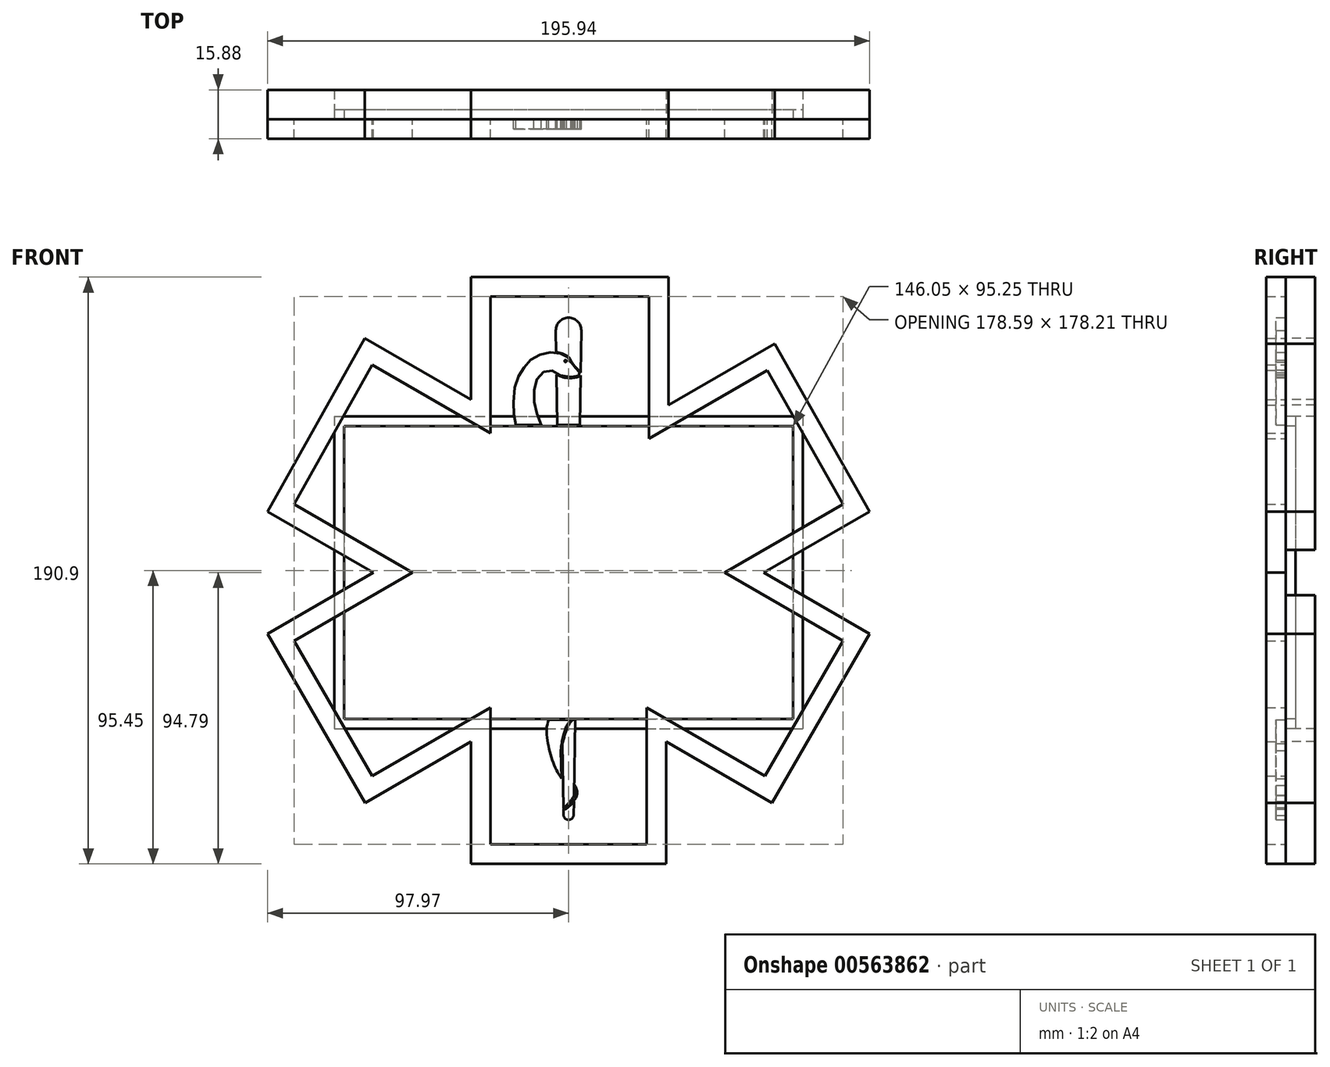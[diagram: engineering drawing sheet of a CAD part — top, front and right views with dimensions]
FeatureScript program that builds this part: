
annotation { "Feature Type Name" : "Feature", "Feature Type Description" : "" }
export const myFeature = defineFeature(function(context is Context, id is Id, definition is map)
    precondition{}
    {
        {
            var Q0;
            Q0=qCreatedBy(makeId("Front.planeOp"),FACE);
            var sketch = newSketch(context, id + "F0", { "sketchPlane" : qUnion([Q0])});
            skLineSegment(sketch, "E0.bottom", {"start": v(-76.2, 50.8) * mm, "end": v(76.2, 50.8) * mm});
            skLineSegment(sketch, "E0.top", {"start": v(-76.2, -50.8) * mm, "end": v(76.2, -50.8) * mm});
            skLineSegment(sketch, "E0.left", {"start": v(-76.2, 50.8) * mm, "end": v(-76.2, -50.8) * mm});
            skLineSegment(sketch, "E0.right", {"start": v(76.2, 50.8) * mm, "end": v(76.2, -50.8) * mm});
            skPoint(sketch, "E0.middle", {"position": v(0, 0) * mm});
            skCircle(sketch, "E1", {"center": v(0, 0) * mm, "radius": 50.8 * mm, "construction": true});
            skPoint(sketch, "E2.endSnap0", {"position": v(0, 50.8) * mm});
            skLineSegment(sketch, "E3", {"start": v(0, 50.8) * mm, "end": v(0, 173.84) * mm, "construction": true});
            skLineSegment(sketch, "E4", {"start": v(0, -50.8) * mm, "end": v(0, -189.44) * mm, "construction": true});
            skPoint(sketch, "E5.endSnap0", {"position": v(-44, 0) * mm});
            skLineSegment(sketch, "E6", {"start": v(-25.4, -44) * mm, "end": v(-25.4, -88.44) * mm});
            skLineSegment(sketch, "E7", {"start": v(-25.4, -88.44) * mm, "end": v(25.4, -88.44) * mm});
            skLineSegment(sketch, "E8", {"start": v(25.4, -88.44) * mm, "end": v(25.4, -44) * mm});
            skLineSegment(sketch, "E9", {"start": v(25.4, -44) * mm, "end": v(63.9, -66.22) * mm});
            skLineSegment(sketch, "E10", {"start": v(50.8, 0) * mm, "end": v(89.3, -22.23) * mm});
            skLineSegment(sketch, "E11", {"start": v(50.8, 0) * mm, "end": v(89.3, 22.23) * mm});
            skLineSegment(sketch, "E12", {"start": v(26.16, 43.55) * mm, "end": v(64.66, 65.77) * mm});
            skLineSegment(sketch, "E13", {"start": v(26.16, 43.55) * mm, "end": v(26.16, 89.76) * mm});
            skLineSegment(sketch, "E14", {"start": v(-25.4, 45.31) * mm, "end": v(-25.4, 89.76) * mm});
            skLineSegment(sketch, "E15", {"start": v(-25.4, 45.31) * mm, "end": v(-63.9, 67.54) * mm});
            skLineSegment(sketch, "E16", {"start": v(-50.8, 0) * mm, "end": v(-89.3, 22.23) * mm});
            skLineSegment(sketch, "E17", {"start": v(-50.8, 0) * mm, "end": v(-89.3, -22.23) * mm});
            skLineSegment(sketch, "E18", {"start": v(-25.4, -44) * mm, "end": v(-63.9, -66.22) * mm});
            skLineSegment(sketch, "E19", {"start": v(-25.4, 89.76) * mm, "end": v(26.16, 89.76) * mm});
            skLineSegment(sketch, "E20", {"start": v(64.66, 65.77) * mm, "end": v(89.3, 22.22) * mm});
            skLineSegment(sketch, "E21", {"start": v(-63.9, 67.54) * mm, "end": v(-89.3, 22.23) * mm});
            skLineSegment(sketch, "E22", {"start": v(-89.3, -22.23) * mm, "end": v(-63.9, -66.22) * mm});
            skLineSegment(sketch, "E23", {"start": v(63.9, -66.22) * mm, "end": v(89.3, -22.23) * mm});
            skLineSegment(sketch, "E24.0", {"start": v(32.51, 54.54) * mm, "end": v(67.03, 74.47) * mm});
            skLineSegment(sketch, "E24.1", {"start": v(67.03, 74.47) * mm, "end": v(97.92, 19.87) * mm});
            skLineSegment(sketch, "E24.2", {"start": v(63.5, 0) * mm, "end": v(97.92, 19.87) * mm});
            skLineSegment(sketch, "E24.3", {"start": v(63.5, 0) * mm, "end": v(97.97, -19.9) * mm});
            skLineSegment(sketch, "E24.4", {"start": v(66.22, -74.9) * mm, "end": v(97.97, -19.9) * mm});
            skLineSegment(sketch, "E24.5", {"start": v(32.51, 54.54) * mm, "end": v(32.51, 96.11) * mm});
            skLineSegment(sketch, "E24.6", {"start": v(31.75, -55) * mm, "end": v(66.22, -74.9) * mm});
            skLineSegment(sketch, "E24.7", {"start": v(31.75, -94.8) * mm, "end": v(31.75, -55) * mm});
            skLineSegment(sketch, "E24.8", {"start": v(-66.29, 76.25) * mm, "end": v(-97.9, 19.86) * mm});
            skLineSegment(sketch, "E24.9", {"start": v(-31.75, 56.31) * mm, "end": v(-66.29, 76.25) * mm});
            skLineSegment(sketch, "E24.10", {"start": v(-31.75, 56.31) * mm, "end": v(-31.75, 96.11) * mm});
            skLineSegment(sketch, "E24.11", {"start": v(-31.75, 96.11) * mm, "end": v(32.51, 96.11) * mm});
            skLineSegment(sketch, "E24.12", {"start": v(-63.5, 0) * mm, "end": v(-97.9, 19.86) * mm});
            skLineSegment(sketch, "E24.13", {"start": v(-63.5, 0) * mm, "end": v(-97.97, -19.9) * mm});
            skLineSegment(sketch, "E24.14", {"start": v(-97.97, -19.9) * mm, "end": v(-66.22, -74.9) * mm});
            skLineSegment(sketch, "E24.15", {"start": v(-31.75, -55) * mm, "end": v(-66.22, -74.9) * mm});
            skLineSegment(sketch, "E24.16", {"start": v(-31.75, -55) * mm, "end": v(-31.75, -94.8) * mm});
            skLineSegment(sketch, "E24.17", {"start": v(-31.75, -94.8) * mm, "end": v(31.75, -94.8) * mm});
            skLineSegment(sketch, "E25.0", {"start": v(-73.03, 47.63) * mm, "end": v(73.02, 47.63) * mm});
            skLineSegment(sketch, "E25.1", {"start": v(-73.03, 47.63) * mm, "end": v(-73.03, -47.62) * mm});
            skLineSegment(sketch, "E25.2", {"start": v(-73.03, -47.62) * mm, "end": v(73.03, -47.62) * mm});
            skLineSegment(sketch, "E25.3", {"start": v(73.02, 47.63) * mm, "end": v(73.02, -47.62) * mm});
            skSolve(sketch);
        }
        {
            var Q0;
            Q0=qCreatedBy(makeId("Front.planeOp"),FACE);
            var sketch = newSketch(context, id + "F1", { "sketchPlane" : qUnion([Q0])});
            skPoint(sketch, "E26", {"position": v(0, 78.78) * mm});
            skArc(sketch, "E27", {"start": v(-4.15, 78.78) * mm, "mid": v(0, 82.92) * mm, "end": v(4.15, 78.78) * mm});
            skArc(sketch, "E28", {"start": v(-1.64, -78.95) * mm, "mid": v(0, -80.43) * mm, "end": v(1.64, -78.96) * mm});
            skPoint(sketch, "E28.centerSnap0", {"position": v(0, 82.92) * mm});
            skLineSegment(sketch, "E29", {"start": v(-4.15, 78.78) * mm, "end": v(-1.64, -78.95) * mm, "construction": true});
            skLineSegment(sketch, "E30", {"start": v(1.64, -78.96) * mm, "end": v(4.15, 78.78) * mm, "construction": true});
            skFitSpline(sketch, "E31", {"points": [v(-8.9, 48.07) * mm, v(-10.84, 53.86) * mm, v(-11.14, 60.19) * mm, v(-9.28, 64.33) * mm, v(-5.74, 65.83) * mm, v(-2.63, 64.08) * mm, v(2.02, 63.68) * mm, v(3.54, 64.19) * mm, v(3.75, 64.86) * mm, v(3.08, 65.8) * mm, v(1.83, 66.97) * mm, v(0.63, 68.77) * mm, v(0, 69.85) * mm, v(-3.16, 71.36) * mm, v(-7.6, 71.36) * mm, v(-12.16, 69.37) * mm, v(-15.04, 65.95) * mm, v(-17.2, 61.39) * mm, v(-17.87, 52.8) * mm, v(-17.15, 48.06) * mm], "startDerivative": vector(-30.37, 85.84) * mm, "endDerivative": vector(17.9, -89.5) * mm});
            skLineSegment(sketch, "E32", {"start": v(-17.15, 48.06) * mm, "end": v(-8.9, 48.07) * mm});
            skCircle(sketch, "E33", {"center": v(-0.99, 68.8) * mm, "radius": 0.33 * mm});
            skLineSegment(sketch, "E34", {"start": v(-3.66, 47.96) * mm, "end": v(-3.92, 64.42) * mm});
            skLineSegment(sketch, "E35", {"start": v(3.66, 47.96) * mm, "end": v(4.15, 78.78) * mm});
            skLineSegment(sketch, "E36", {"start": v(-4.15, 78.78) * mm, "end": v(-4.03, 71.63) * mm});
            skFitSpline(sketch, "E37", {"points": [v(-3.92, 64.42) * mm, v(-3.09, 64) * mm, v(-1.88, 63.55) * mm, v(-0.5, 63.32) * mm, v(1, 63.3) * mm, v(2.62, 63.52) * mm, v(3.6, 63.87) * mm, v(3.91, 64.11) * mm, v(3.91, 64.11) * mm], "startDerivative": vector(5.71, -3.81) * mm, "endDerivative": vector(-0.08, -0.33) * mm});
            skFitSpline(sketch, "E38", {"points": [v(-4.03, 71.63) * mm, v(-2.9, 71.5) * mm, v(-1.65, 71.08) * mm, v(-0.43, 70.42) * mm, v(0.33, 69.76) * mm, v(0.77, 68.92) * mm, v(1.23, 68.05) * mm, v(1.8, 67.3) * mm, v(2.8, 66.26) * mm, v(3.24, 65.86) * mm, v(3.7, 65.35) * mm, v(3.93, 64.98) * mm], "startDerivative": vector(10.65, -1.85) * mm, "endDerivative": vector(3.06, -5.8) * mm});
            skLineSegment(sketch, "E39", {"start": v(-3.66, 47.96) * mm, "end": v(3.66, 47.96) * mm});
            skFitSpline(sketch, "E40", {"points": [v(-1.4, -76.5) * mm, v(-0.47, -75.73) * mm, v(0.47, -74.71) * mm, v(1.3, -73.6) * mm, v(1.94, -72.45) * mm], "startDerivative": vector(4.24, 2.97) * mm, "endDerivative": vector(1.93, 4.13) * mm});
            skLineSegment(sketch, "E41", {"start": v(1.94, -72.45) * mm, "end": v(1.99, -69.23) * mm});
            skFitSpline(sketch, "E42", {"points": [v(1.99, -69.23) * mm, v(2.42, -69.9) * mm, v(2.72, -70.7) * mm, v(2.85, -71.7) * mm, v(2.67, -72.61) * mm, v(2.27, -73.42) * mm, v(1.5, -74.5) * mm, v(0.52, -75.54) * mm, v(-0.54, -76.42) * mm, v(-1.4, -76.88) * mm, v(-1.68, -76.68) * mm, v(-1.4, -76.5) * mm], "startDerivative": vector(6.4, -7.49) * mm, "endDerivative": vector(7.48, 2.6) * mm});
            skFitSpline(sketch, "E43", {"points": [v(-2.26, -67.04) * mm, v(-4.04, -63.98) * mm, v(-5.65, -60.1) * mm, v(-6.71, -55.55) * mm, v(-7.17, -51.16) * mm, v(-6.5, -47.92) * mm], "startDerivative": vector(-10.74, 15.93) * mm, "endDerivative": vector(4.95, 17.16) * mm});
            skLineSegment(sketch, "E44", {"start": v(-2.26, -67.04) * mm, "end": v(-2.53, -57.92) * mm});
            skFitSpline(sketch, "E45", {"points": [v(-2.53, -57.92) * mm, v(-1.84, -53.56) * mm, v(-1.18, -51.24) * mm, v(-0.22, -49.14) * mm, v(0.76, -47.85) * mm], "startDerivative": vector(1.14, 14.17) * mm, "endDerivative": vector(5.1, 5.9) * mm});
            skLineSegment(sketch, "E46", {"start": v(-6.5, -47.92) * mm, "end": v(0.76, -47.85) * mm});
            skLineSegment(sketch, "E47", {"start": v(-1.68, -76.9) * mm, "end": v(-1.64, -78.95) * mm});
            skLineSegment(sketch, "E48", {"start": v(1.64, -78.96) * mm, "end": v(1.71, -74.44) * mm});
            skLineSegment(sketch, "E49", {"start": v(-2.01, -55.65) * mm, "end": v(-1.68, -76.52) * mm});
            skLineSegment(sketch, "E50", {"start": v(1.74, -72.55) * mm, "end": v(2.14, -47.85) * mm});
            skLineSegment(sketch, "E51", {"start": v(1.3, -47.85) * mm, "end": v(2.14, -47.85) * mm});
            skFitSpline(sketch, "E52", {"points": [v(1.3, -47.85) * mm, v(0.26, -49.22) * mm, v(-0.63, -51.11) * mm, v(-1.28, -53.06) * mm, v(-2.01, -55.65) * mm], "startDerivative": vector(-4.84, -5.67) * mm, "endDerivative": vector(-2.62, -9.58) * mm});
            skFitSpline(sketch, "E53", {"points": [v(1.74, -72.55) * mm, v(1.2, -73.44) * mm, v(0.62, -74.27) * mm, v(0.07, -74.95) * mm, v(-0.44, -75.47) * mm, v(-0.86, -75.92) * mm, v(-1.68, -76.52) * mm], "startDerivative": vector(-2.86, -4.93) * mm, "endDerivative": vector(-5.02, -3.44) * mm});
            skFitSpline(sketch, "E54", {"points": [v(-1.68, -76.9) * mm, v(-1.5, -77) * mm, v(-1.18, -76.98) * mm, v(-0.5, -76.58) * mm, v(0.44, -75.8) * mm, v(1.12, -75.17) * mm, v(1.71, -74.44) * mm], "startDerivative": vector(1.8, -1.13) * mm, "endDerivative": vector(2.96, 3.86) * mm});
            skSolve(sketch);
        }
        {
            var Q0;
            {var subQ5=sQuery(id+"F0.wireOp",EDGE,"E19");Q0=makeQuery(id+"F0.imprint","IMPRINT",FACE,{"disambiguationData":[TD([[makeQuery(id+"F0.imprint","IMPRINT",EDGE,{"derivedFrom":subQ5}),-1.0]])]});}
            var Q1;
            {var subQ10=sQuery(id+"F0.wireOp",EDGE,"E19");Q1=makeQuery(id+"F0.imprint","IMPRINT",FACE,{"disambiguationData":[TD([[makeQuery(id+"F0.imprint","IMPRINT",EDGE,{"derivedFrom":subQ10}),1.0]])]});}
            var Q2;
            {var subQ0=sQuery(id+"F0.wireOp",EDGE,"E21");var subQ1=sQuery(id+"F0.wireOp",EDGE,"E0.bottom");var subQ2=makeQuery(id+"F0.imprint","INTERSECT",VERTEX,{"derivedFrom":[subQ1,subQ0]});Q2=makeQuery(id+"F0.imprint","IMPRINT",FACE,{"disambiguationData":[TD([[makeQuery(id+"F0.imprint","IMPRINT",EDGE,{"disambiguationData":[TD([[subQ2,-1.0]])],"derivedFrom":subQ1}),1.0]])]});}
            var Q3;
            {var subQ0=sQuery(id+"F0.wireOp",EDGE,"E21");var subQ1=sQuery(id+"F0.wireOp",EDGE,"E0.left");var subQ2=makeQuery(id+"F0.imprint","INTERSECT",VERTEX,{"derivedFrom":[subQ1,subQ0]});Q3=makeQuery(id+"F0.imprint","IMPRINT",FACE,{"disambiguationData":[TD([[makeQuery(id+"F0.imprint","IMPRINT",EDGE,{"disambiguationData":[TD([[subQ2,-1.0]])],"derivedFrom":subQ1}),-1.0]])]});}
            var Q4;
            {var subQ26=sQuery(id+"F0.wireOp",EDGE,"E7");Q4=makeQuery(id+"F0.imprint","IMPRINT",FACE,{"disambiguationData":[TD([[makeQuery(id+"F0.imprint","IMPRINT",EDGE,{"derivedFrom":subQ26}),-1.0]])]});}
            var Q5;
            {var subQ0=sQuery(id+"F0.wireOp",EDGE,"E17");var subQ1=sQuery(id+"F0.wireOp",EDGE,"E0.left");var subQ2=makeQuery(id+"F0.imprint","INTERSECT",VERTEX,{"derivedFrom":[subQ1,subQ0]});Q5=makeQuery(id+"F0.imprint","IMPRINT",FACE,{"disambiguationData":[TD([[makeQuery(id+"F0.imprint","IMPRINT",EDGE,{"disambiguationData":[TD([[subQ2,-1.0]])],"derivedFrom":subQ1}),-1.0]])]});}
            var Q6;
            {var subQ0=sQuery(id+"F0.wireOp",EDGE,"E22");var subQ1=sQuery(id+"F0.wireOp",EDGE,"E0.top");var subQ2=makeQuery(id+"F0.imprint","INTERSECT",VERTEX,{"derivedFrom":[subQ1,subQ0]});Q6=makeQuery(id+"F0.imprint","IMPRINT",FACE,{"disambiguationData":[TD([[makeQuery(id+"F0.imprint","IMPRINT",EDGE,{"disambiguationData":[TD([[subQ2,-1.0]])],"derivedFrom":subQ1}),-1.0]])]});}
            var Q7;
            {var subQ5=sQuery(id+"F0.wireOp",EDGE,"E7");Q7=makeQuery(id+"F0.imprint","IMPRINT",FACE,{"disambiguationData":[TD([[makeQuery(id+"F0.imprint","IMPRINT",EDGE,{"derivedFrom":subQ5}),1.0]])]});}
            var Q8;
            {var subQ0=sQuery(id+"F0.wireOp",EDGE,"E9");var subQ1=sQuery(id+"F0.wireOp",EDGE,"E0.top");var subQ2=makeQuery(id+"F0.imprint","INTERSECT",VERTEX,{"derivedFrom":[subQ1,subQ0]});Q8=makeQuery(id+"F0.imprint","IMPRINT",FACE,{"disambiguationData":[TD([[makeQuery(id+"F0.imprint","IMPRINT",EDGE,{"disambiguationData":[TD([[subQ2,-1.0]])],"derivedFrom":subQ1}),-1.0]])]});}
            var Q9;
            {var subQ0=sQuery(id+"F0.wireOp",EDGE,"E10");var subQ1=sQuery(id+"F0.wireOp",EDGE,"E0.right");var subQ2=makeQuery(id+"F0.imprint","INTERSECT",VERTEX,{"derivedFrom":[subQ1,subQ0]});Q9=makeQuery(id+"F0.imprint","IMPRINT",FACE,{"disambiguationData":[TD([[makeQuery(id+"F0.imprint","IMPRINT",EDGE,{"disambiguationData":[TD([[subQ2,-1.0]])],"derivedFrom":subQ1}),1.0]])]});}
            var Q10;
            {var subQ0=sQuery(id+"F0.wireOp",EDGE,"E20");var subQ1=sQuery(id+"F0.wireOp",EDGE,"E0.right");var subQ2=makeQuery(id+"F0.imprint","INTERSECT",VERTEX,{"derivedFrom":[subQ1,subQ0]});Q10=makeQuery(id+"F0.imprint","IMPRINT",FACE,{"disambiguationData":[TD([[makeQuery(id+"F0.imprint","IMPRINT",EDGE,{"disambiguationData":[TD([[subQ2,-1.0]])],"derivedFrom":subQ1}),1.0]])]});}
            var Q11;
            {var subQ0=sQuery(id+"F0.wireOp",EDGE,"E12");var subQ1=sQuery(id+"F0.wireOp",EDGE,"E0.bottom");var subQ2=makeQuery(id+"F0.imprint","INTERSECT",VERTEX,{"derivedFrom":[subQ1,subQ0]});Q11=makeQuery(id+"F0.imprint","IMPRINT",FACE,{"disambiguationData":[TD([[makeQuery(id+"F0.imprint","IMPRINT",EDGE,{"disambiguationData":[TD([[subQ2,-1.0]])],"derivedFrom":subQ1}),1.0]])]});}
            extrude(context, id + "F2", {"entities" : qUnion([Q0, Q1, Q2, Q3, Q4, Q5, Q6, Q7, Q8, Q9, Q10, Q11]), "oppositeDirection" : true, "depth" : 9.52 * mm, "offsetDistance" : 25.4 * mm});
        }
        {
            var Q0;
            Q0 = qSketchRegion(id + "F1", true);
            extrude(context, id + "F3", {"entities" : qUnion([Q0]), "depth" : 3.17 * mm, "offsetDistance" : 25.4 * mm});
        }
        {
            var Q0;
            {var subQ10=sQuery(id+"F0.wireOp",EDGE,"E19");Q0=makeQuery(id+"F0.imprint","IMPRINT",FACE,{"disambiguationData":[TD([[makeQuery(id+"F0.imprint","IMPRINT",EDGE,{"derivedFrom":subQ10}),1.0]])]});}
            var Q1;
            {var subQ0=sQuery(id+"F0.wireOp",EDGE,"E15");var subQ1=sQuery(id+"F0.wireOp",EDGE,"E0.bottom");var subQ2=makeQuery(id+"F0.imprint","INTERSECT",VERTEX,{"derivedFrom":[subQ1,subQ0]});Q1=makeQuery(id+"F0.imprint","IMPRINT",FACE,{"disambiguationData":[TD([[makeQuery(id+"F0.imprint","IMPRINT",EDGE,{"disambiguationData":[TD([[subQ2,-1.0]])],"derivedFrom":subQ1}),-1.0]])]});}
            var Q2;
            {var subQ0=sQuery(id+"F0.wireOp",EDGE,"E15");var subQ1=sQuery(id+"F0.wireOp",EDGE,"E14");var subQ2=makeQuery(id+"F0.imprint","INTERSECT",VERTEX,{"derivedFrom":[subQ1,subQ0]});Q2=makeQuery(id+"F0.imprint","IMPRINT",FACE,{"disambiguationData":[TD([[makeQuery(id+"F0.imprint","IMPRINT",EDGE,{"disambiguationData":[TD([[subQ2,-1.0]])],"derivedFrom":subQ1}),1.0]])]});}
            var Q3;
            {var subQ0=sQuery(id+"F0.wireOp",EDGE,"E0.left");var subQ1=sQuery(id+"F0.wireOp",EDGE,"E0.bottom");var subQ2=makeQuery(id+"F0.imprint","INTERSECT",VERTEX,{"derivedFrom":[subQ1,subQ0]});Q3=makeQuery(id+"F0.imprint","IMPRINT",FACE,{"disambiguationData":[TD([[makeQuery(id+"F0.imprint","IMPRINT",EDGE,{"disambiguationData":[TD([[subQ2,-1.0]])],"derivedFrom":subQ1}),-1.0]])]});}
            var Q4;
            {var subQ6=sQuery(id+"F0.wireOp",EDGE,"E17");var subQ7=sQuery(id+"F0.wireOp",EDGE,"E16");var subQ8=makeQuery(id+"F0.imprint","INTERSECT",VERTEX,{"derivedFrom":[subQ7,subQ6]});Q4=makeQuery(id+"F0.imprint","IMPRINT",FACE,{"disambiguationData":[TD([[makeQuery(id+"F0.imprint","IMPRINT",EDGE,{"disambiguationData":[TD([[subQ8,-1.0]])],"derivedFrom":subQ7}),1.0]])]});}
            var Q5;
            {var subQ0=sQuery(id+"F0.wireOp",EDGE,"E24.12");var subQ1=sQuery(id+"F0.wireOp",EDGE,"E0.left");var subQ2=makeQuery(id+"F0.imprint","INTERSECT",VERTEX,{"derivedFrom":[subQ1,subQ0]});Q5=makeQuery(id+"F0.imprint","IMPRINT",FACE,{"disambiguationData":[TD([[makeQuery(id+"F0.imprint","IMPRINT",EDGE,{"disambiguationData":[TD([[subQ2,1.0]])],"derivedFrom":subQ1}),1.0]])]});}
            var Q6;
            {var subQ0=sQuery(id+"F0.wireOp",EDGE,"E24.13");var subQ1=sQuery(id+"F0.wireOp",EDGE,"E0.left");var subQ2=makeQuery(id+"F0.imprint","INTERSECT",VERTEX,{"derivedFrom":[subQ1,subQ0]});Q6=makeQuery(id+"F0.imprint","IMPRINT",FACE,{"disambiguationData":[TD([[makeQuery(id+"F0.imprint","IMPRINT",EDGE,{"disambiguationData":[TD([[subQ2,-1.0]])],"derivedFrom":subQ1}),1.0]])]});}
            var Q7;
            {var subQ26=sQuery(id+"F0.wireOp",EDGE,"E7");Q7=makeQuery(id+"F0.imprint","IMPRINT",FACE,{"disambiguationData":[TD([[makeQuery(id+"F0.imprint","IMPRINT",EDGE,{"derivedFrom":subQ26}),-1.0]])]});}
            var Q8;
            {var subQ0=sQuery(id+"F0.wireOp",EDGE,"E18");var subQ1=sQuery(id+"F0.wireOp",EDGE,"E6");var subQ2=makeQuery(id+"F0.imprint","INTERSECT",VERTEX,{"derivedFrom":[subQ1,subQ0]});Q8=makeQuery(id+"F0.imprint","IMPRINT",FACE,{"disambiguationData":[TD([[makeQuery(id+"F0.imprint","IMPRINT",EDGE,{"disambiguationData":[TD([[subQ2,-1.0]])],"derivedFrom":subQ1}),-1.0]])]});}
            var Q9;
            {var subQ0=sQuery(id+"F0.wireOp",EDGE,"E18");var subQ1=sQuery(id+"F0.wireOp",EDGE,"E0.top");var subQ2=makeQuery(id+"F0.imprint","INTERSECT",VERTEX,{"derivedFrom":[subQ1,subQ0]});Q9=makeQuery(id+"F0.imprint","IMPRINT",FACE,{"disambiguationData":[TD([[makeQuery(id+"F0.imprint","IMPRINT",EDGE,{"disambiguationData":[TD([[subQ2,-1.0]])],"derivedFrom":subQ1}),1.0]])]});}
            var Q10;
            {var subQ0=sQuery(id+"F0.wireOp",EDGE,"E0.left");var subQ1=sQuery(id+"F0.wireOp",EDGE,"E0.top");var subQ2=makeQuery(id+"F0.imprint","INTERSECT",VERTEX,{"derivedFrom":[subQ1,subQ0]});Q10=makeQuery(id+"F0.imprint","IMPRINT",FACE,{"disambiguationData":[TD([[makeQuery(id+"F0.imprint","IMPRINT",EDGE,{"disambiguationData":[TD([[subQ2,-1.0]])],"derivedFrom":subQ1}),1.0]])]});}
            var Q11;
            {var subQ0=sQuery(id+"F0.wireOp",EDGE,"E8");var subQ1=sQuery(id+"F0.wireOp",EDGE,"E0.top");var subQ2=makeQuery(id+"F0.imprint","INTERSECT",VERTEX,{"derivedFrom":[subQ1,subQ0]});Q11=makeQuery(id+"F0.imprint","IMPRINT",FACE,{"disambiguationData":[TD([[makeQuery(id+"F0.imprint","IMPRINT",EDGE,{"disambiguationData":[TD([[subQ2,-1.0]])],"derivedFrom":subQ1}),1.0]])]});}
            var Q12;
            {var subQ0=sQuery(id+"F0.wireOp",EDGE,"E9");var subQ1=sQuery(id+"F0.wireOp",EDGE,"E8");var subQ2=makeQuery(id+"F0.imprint","INTERSECT",VERTEX,{"derivedFrom":[subQ1,subQ0]});Q12=makeQuery(id+"F0.imprint","IMPRINT",FACE,{"disambiguationData":[TD([[makeQuery(id+"F0.imprint","IMPRINT",EDGE,{"disambiguationData":[TD([[subQ2,1.0]])],"derivedFrom":subQ1}),-1.0]])]});}
            var Q13;
            {var subQ5=sQuery(id+"F0.wireOp",EDGE,"E11");var subQ6=sQuery(id+"F0.wireOp",EDGE,"E10");var subQ7=makeQuery(id+"F0.imprint","INTERSECT",VERTEX,{"derivedFrom":[subQ6,subQ5]});Q13=makeQuery(id+"F0.imprint","IMPRINT",FACE,{"disambiguationData":[TD([[makeQuery(id+"F0.imprint","IMPRINT",EDGE,{"disambiguationData":[TD([[subQ7,-1.0]])],"derivedFrom":subQ6}),1.0]])]});}
            var Q14;
            {var subQ0=sQuery(id+"F0.wireOp",EDGE,"E24.3");var subQ1=sQuery(id+"F0.wireOp",EDGE,"E0.right");var subQ2=makeQuery(id+"F0.imprint","INTERSECT",VERTEX,{"derivedFrom":[subQ1,subQ0]});Q14=makeQuery(id+"F0.imprint","IMPRINT",FACE,{"disambiguationData":[TD([[makeQuery(id+"F0.imprint","IMPRINT",EDGE,{"disambiguationData":[TD([[subQ2,-1.0]])],"derivedFrom":subQ1}),-1.0]])]});}
            var Q15;
            {var subQ0=sQuery(id+"F0.wireOp",EDGE,"E24.2");var subQ1=sQuery(id+"F0.wireOp",EDGE,"E0.right");var subQ2=makeQuery(id+"F0.imprint","INTERSECT",VERTEX,{"derivedFrom":[subQ1,subQ0]});Q15=makeQuery(id+"F0.imprint","IMPRINT",FACE,{"disambiguationData":[TD([[makeQuery(id+"F0.imprint","IMPRINT",EDGE,{"disambiguationData":[TD([[subQ2,1.0]])],"derivedFrom":subQ1}),-1.0]])]});}
            var Q16;
            {var subQ0=sQuery(id+"F0.wireOp",EDGE,"E0.right");var subQ1=sQuery(id+"F0.wireOp",EDGE,"E0.bottom");var subQ2=makeQuery(id+"F0.imprint","INTERSECT",VERTEX,{"derivedFrom":[subQ1,subQ0]});Q16=makeQuery(id+"F0.imprint","IMPRINT",FACE,{"disambiguationData":[TD([[makeQuery(id+"F0.imprint","IMPRINT",EDGE,{"disambiguationData":[TD([[subQ2,1.0]])],"derivedFrom":subQ1}),-1.0]])]});}
            var Q17;
            {var subQ0=sQuery(id+"F0.wireOp",EDGE,"E13");var subQ1=sQuery(id+"F0.wireOp",EDGE,"E0.bottom");var subQ2=makeQuery(id+"F0.imprint","INTERSECT",VERTEX,{"derivedFrom":[subQ1,subQ0]});Q17=makeQuery(id+"F0.imprint","IMPRINT",FACE,{"disambiguationData":[TD([[makeQuery(id+"F0.imprint","IMPRINT",EDGE,{"disambiguationData":[TD([[subQ2,-1.0]])],"derivedFrom":subQ1}),-1.0]])]});}
            var Q18;
            {var subQ0=sQuery(id+"F0.wireOp",EDGE,"E13");var subQ1=sQuery(id+"F0.wireOp",EDGE,"E12");var subQ2=makeQuery(id+"F0.imprint","INTERSECT",VERTEX,{"derivedFrom":[subQ1,subQ0]});Q18=makeQuery(id+"F0.imprint","IMPRINT",FACE,{"disambiguationData":[TD([[makeQuery(id+"F0.imprint","IMPRINT",EDGE,{"disambiguationData":[TD([[subQ2,-1.0]])],"derivedFrom":subQ1}),1.0]])]});}
            var Q19;
            {var subQ0=sQuery(id+"F0.wireOp",EDGE,"E0.right");var subQ1=sQuery(id+"F0.wireOp",EDGE,"E0.top");var subQ2=makeQuery(id+"F0.imprint","INTERSECT",VERTEX,{"derivedFrom":[subQ1,subQ0]});Q19=makeQuery(id+"F0.imprint","IMPRINT",FACE,{"disambiguationData":[TD([[makeQuery(id+"F0.imprint","IMPRINT",EDGE,{"disambiguationData":[TD([[subQ2,1.0]])],"derivedFrom":subQ1}),1.0]])]});}
            extrude(context, id + "F4", {"entities" : qUnion([Q0, Q1, Q2, Q3, Q4, Q5, Q6, Q7, Q8, Q9, Q10, Q11, Q12, Q13, Q14, Q15, Q16, Q17, Q18, Q19]), "depth" : 6.35 * mm, "offsetDistance" : 25.4 * mm});
        }
        {
            var Q0;
            {var subQ0=sQuery(id+"F0.wireOp",EDGE,"E14");var subQ1=sQuery(id+"F0.wireOp",EDGE,"E0.bottom");var subQ2=makeQuery(id+"F0.imprint","INTERSECT",VERTEX,{"derivedFrom":[subQ1,subQ0]});Q0=makeQuery(id+"F0.imprint","IMPRINT",FACE,{"disambiguationData":[TD([[makeQuery(id+"F0.imprint","IMPRINT",EDGE,{"disambiguationData":[TD([[subQ2,-1.0]])],"derivedFrom":subQ1}),-1.0]])]});}
            var Q1;
            {var subQ0=sQuery(id+"F0.wireOp",EDGE,"E15");var subQ1=sQuery(id+"F0.wireOp",EDGE,"E0.bottom");var subQ2=makeQuery(id+"F0.imprint","INTERSECT",VERTEX,{"derivedFrom":[subQ1,subQ0]});Q1=makeQuery(id+"F0.imprint","IMPRINT",FACE,{"disambiguationData":[TD([[makeQuery(id+"F0.imprint","IMPRINT",EDGE,{"disambiguationData":[TD([[subQ2,-1.0]])],"derivedFrom":subQ1}),-1.0]])]});}
            var Q2;
            {var subQ6=sQuery(id+"F0.wireOp",EDGE,"E0.bottom");var subQ11=sQuery(id+"F0.wireOp",EDGE,"E21");var subQ13=makeQuery(id+"F0.imprint","INTERSECT",VERTEX,{"derivedFrom":[subQ6,subQ11]});Q2=makeQuery(id+"F0.imprint","IMPRINT",FACE,{"disambiguationData":[TD([[makeQuery(id+"F0.imprint","IMPRINT",EDGE,{"disambiguationData":[TD([[subQ13,-1.0]])],"derivedFrom":subQ6}),-1.0]])]});}
            var Q3;
            {var subQ0=sQuery(id+"F0.wireOp",EDGE,"E0.left");var subQ1=sQuery(id+"F0.wireOp",EDGE,"E0.bottom");var subQ2=makeQuery(id+"F0.imprint","INTERSECT",VERTEX,{"derivedFrom":[subQ1,subQ0]});Q3=makeQuery(id+"F0.imprint","IMPRINT",FACE,{"disambiguationData":[TD([[makeQuery(id+"F0.imprint","IMPRINT",EDGE,{"disambiguationData":[TD([[subQ2,-1.0]])],"derivedFrom":subQ1}),-1.0]])]});}
            var Q4;
            {var subQ0=sQuery(id+"F0.wireOp",EDGE,"E24.12");var subQ1=sQuery(id+"F0.wireOp",EDGE,"E0.left");var subQ2=makeQuery(id+"F0.imprint","INTERSECT",VERTEX,{"derivedFrom":[subQ1,subQ0]});Q4=makeQuery(id+"F0.imprint","IMPRINT",FACE,{"disambiguationData":[TD([[makeQuery(id+"F0.imprint","IMPRINT",EDGE,{"disambiguationData":[TD([[subQ2,1.0]])],"derivedFrom":subQ1}),1.0]])]});}
            var Q5;
            {var subQ0=sQuery(id+"F0.wireOp",EDGE,"E24.12");var subQ1=sQuery(id+"F0.wireOp",EDGE,"E0.left");var subQ2=makeQuery(id+"F0.imprint","INTERSECT",VERTEX,{"derivedFrom":[subQ1,subQ0]});Q5=makeQuery(id+"F0.imprint","IMPRINT",FACE,{"disambiguationData":[TD([[makeQuery(id+"F0.imprint","IMPRINT",EDGE,{"disambiguationData":[TD([[subQ2,-1.0]])],"derivedFrom":subQ1}),1.0]])]});}
            var Q6;
            {var subQ0=sQuery(id+"F0.wireOp",EDGE,"E24.13");var subQ1=sQuery(id+"F0.wireOp",EDGE,"E0.left");var subQ2=makeQuery(id+"F0.imprint","INTERSECT",VERTEX,{"derivedFrom":[subQ1,subQ0]});Q6=makeQuery(id+"F0.imprint","IMPRINT",FACE,{"disambiguationData":[TD([[makeQuery(id+"F0.imprint","IMPRINT",EDGE,{"disambiguationData":[TD([[subQ2,-1.0]])],"derivedFrom":subQ1}),1.0]])]});}
            var Q7;
            {var subQ5=sQuery(id+"F0.wireOp",EDGE,"E22");var subQ8=sQuery(id+"F0.wireOp",EDGE,"E0.top");var subQ12=makeQuery(id+"F0.imprint","INTERSECT",VERTEX,{"derivedFrom":[subQ8,subQ5]});Q7=makeQuery(id+"F0.imprint","IMPRINT",FACE,{"disambiguationData":[TD([[makeQuery(id+"F0.imprint","IMPRINT",EDGE,{"disambiguationData":[TD([[subQ12,-1.0]])],"derivedFrom":subQ8}),1.0]])]});}
            var Q8;
            {var subQ0=sQuery(id+"F0.wireOp",EDGE,"E0.left");var subQ1=sQuery(id+"F0.wireOp",EDGE,"E0.top");var subQ2=makeQuery(id+"F0.imprint","INTERSECT",VERTEX,{"derivedFrom":[subQ1,subQ0]});Q8=makeQuery(id+"F0.imprint","IMPRINT",FACE,{"disambiguationData":[TD([[makeQuery(id+"F0.imprint","IMPRINT",EDGE,{"disambiguationData":[TD([[subQ2,-1.0]])],"derivedFrom":subQ1}),1.0]])]});}
            var Q9;
            {var subQ0=sQuery(id+"F0.wireOp",EDGE,"E18");var subQ1=sQuery(id+"F0.wireOp",EDGE,"E0.top");var subQ2=makeQuery(id+"F0.imprint","INTERSECT",VERTEX,{"derivedFrom":[subQ1,subQ0]});Q9=makeQuery(id+"F0.imprint","IMPRINT",FACE,{"disambiguationData":[TD([[makeQuery(id+"F0.imprint","IMPRINT",EDGE,{"disambiguationData":[TD([[subQ2,-1.0]])],"derivedFrom":subQ1}),1.0]])]});}
            var Q10;
            {var subQ0=sQuery(id+"F0.wireOp",EDGE,"E6");var subQ1=sQuery(id+"F0.wireOp",EDGE,"E0.top");var subQ2=makeQuery(id+"F0.imprint","INTERSECT",VERTEX,{"derivedFrom":[subQ1,subQ0]});Q10=makeQuery(id+"F0.imprint","IMPRINT",FACE,{"disambiguationData":[TD([[makeQuery(id+"F0.imprint","IMPRINT",EDGE,{"disambiguationData":[TD([[subQ2,-1.0]])],"derivedFrom":subQ1}),1.0]])]});}
            var Q11;
            {var subQ0=sQuery(id+"F0.wireOp",EDGE,"E8");var subQ1=sQuery(id+"F0.wireOp",EDGE,"E0.top");var subQ2=makeQuery(id+"F0.imprint","INTERSECT",VERTEX,{"derivedFrom":[subQ1,subQ0]});Q11=makeQuery(id+"F0.imprint","IMPRINT",FACE,{"disambiguationData":[TD([[makeQuery(id+"F0.imprint","IMPRINT",EDGE,{"disambiguationData":[TD([[subQ2,-1.0]])],"derivedFrom":subQ1}),1.0]])]});}
            var Q12;
            {var subQ5=sQuery(id+"F0.wireOp",EDGE,"E9");var subQ6=sQuery(id+"F0.wireOp",EDGE,"E0.top");var subQ7=makeQuery(id+"F0.imprint","INTERSECT",VERTEX,{"derivedFrom":[subQ6,subQ5]});Q12=makeQuery(id+"F0.imprint","IMPRINT",FACE,{"disambiguationData":[TD([[makeQuery(id+"F0.imprint","IMPRINT",EDGE,{"disambiguationData":[TD([[subQ7,-1.0]])],"derivedFrom":subQ6}),1.0]])]});}
            var Q13;
            {var subQ0=sQuery(id+"F0.wireOp",EDGE,"E0.right");var subQ1=sQuery(id+"F0.wireOp",EDGE,"E0.top");var subQ2=makeQuery(id+"F0.imprint","INTERSECT",VERTEX,{"derivedFrom":[subQ1,subQ0]});Q13=makeQuery(id+"F0.imprint","IMPRINT",FACE,{"disambiguationData":[TD([[makeQuery(id+"F0.imprint","IMPRINT",EDGE,{"disambiguationData":[TD([[subQ2,1.0]])],"derivedFrom":subQ1}),1.0]])]});}
            var Q14;
            {var subQ0=sQuery(id+"F0.wireOp",EDGE,"E24.3");var subQ1=sQuery(id+"F0.wireOp",EDGE,"E0.right");var subQ2=makeQuery(id+"F0.imprint","INTERSECT",VERTEX,{"derivedFrom":[subQ1,subQ0]});Q14=makeQuery(id+"F0.imprint","IMPRINT",FACE,{"disambiguationData":[TD([[makeQuery(id+"F0.imprint","IMPRINT",EDGE,{"disambiguationData":[TD([[subQ2,-1.0]])],"derivedFrom":subQ1}),-1.0]])]});}
            var Q15;
            {var subQ0=sQuery(id+"F0.wireOp",EDGE,"E24.2");var subQ1=sQuery(id+"F0.wireOp",EDGE,"E0.right");var subQ2=makeQuery(id+"F0.imprint","INTERSECT",VERTEX,{"derivedFrom":[subQ1,subQ0]});Q15=makeQuery(id+"F0.imprint","IMPRINT",FACE,{"disambiguationData":[TD([[makeQuery(id+"F0.imprint","IMPRINT",EDGE,{"disambiguationData":[TD([[subQ2,-1.0]])],"derivedFrom":subQ1}),-1.0]])]});}
            var Q16;
            {var subQ0=sQuery(id+"F0.wireOp",EDGE,"E24.2");var subQ1=sQuery(id+"F0.wireOp",EDGE,"E0.right");var subQ2=makeQuery(id+"F0.imprint","INTERSECT",VERTEX,{"derivedFrom":[subQ1,subQ0]});Q16=makeQuery(id+"F0.imprint","IMPRINT",FACE,{"disambiguationData":[TD([[makeQuery(id+"F0.imprint","IMPRINT",EDGE,{"disambiguationData":[TD([[subQ2,1.0]])],"derivedFrom":subQ1}),-1.0]])]});}
            var Q17;
            {var subQ7=sQuery(id+"F0.wireOp",EDGE,"E12");var subQ11=sQuery(id+"F0.wireOp",EDGE,"E0.bottom");var subQ12=makeQuery(id+"F0.imprint","INTERSECT",VERTEX,{"derivedFrom":[subQ11,subQ7]});Q17=makeQuery(id+"F0.imprint","IMPRINT",FACE,{"disambiguationData":[TD([[makeQuery(id+"F0.imprint","IMPRINT",EDGE,{"disambiguationData":[TD([[subQ12,-1.0]])],"derivedFrom":subQ11}),-1.0]])]});}
            var Q18;
            {var subQ0=sQuery(id+"F0.wireOp",EDGE,"E0.right");var subQ1=sQuery(id+"F0.wireOp",EDGE,"E0.bottom");var subQ2=makeQuery(id+"F0.imprint","INTERSECT",VERTEX,{"derivedFrom":[subQ1,subQ0]});Q18=makeQuery(id+"F0.imprint","IMPRINT",FACE,{"disambiguationData":[TD([[makeQuery(id+"F0.imprint","IMPRINT",EDGE,{"disambiguationData":[TD([[subQ2,1.0]])],"derivedFrom":subQ1}),-1.0]])]});}
            var Q19;
            {var subQ0=sQuery(id+"F0.wireOp",EDGE,"E13");var subQ1=sQuery(id+"F0.wireOp",EDGE,"E0.bottom");var subQ2=makeQuery(id+"F0.imprint","INTERSECT",VERTEX,{"derivedFrom":[subQ1,subQ0]});Q19=makeQuery(id+"F0.imprint","IMPRINT",FACE,{"disambiguationData":[TD([[makeQuery(id+"F0.imprint","IMPRINT",EDGE,{"disambiguationData":[TD([[subQ2,-1.0]])],"derivedFrom":subQ1}),-1.0]])]});}
            extrude(context, id + "F5", {"entities" : qUnion([Q0, Q1, Q2, Q3, Q4, Q5, Q6, Q7, Q8, Q9, Q10, Q11, Q12, Q13, Q14, Q15, Q16, Q17, Q18, Q19]), "oppositeDirection" : true, "depth" : 3.17 * mm, "offsetDistance" : 25.4 * mm});
        }
    });
